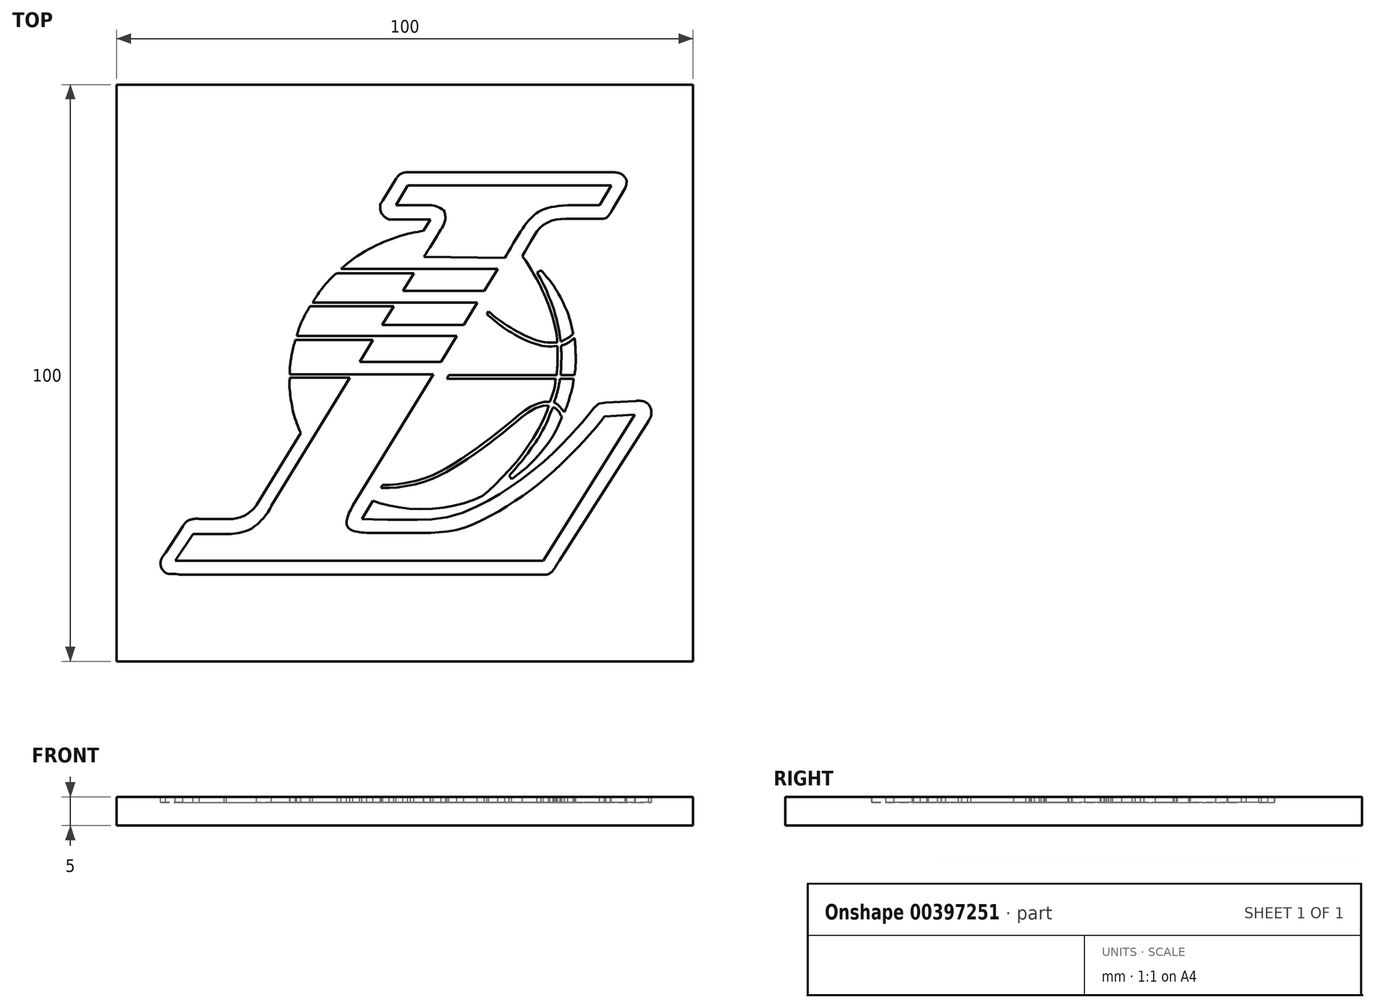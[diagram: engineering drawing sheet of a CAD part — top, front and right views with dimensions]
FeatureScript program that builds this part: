
annotation { "Feature Type Name" : "Feature", "Feature Type Description" : "" }
export const myFeature = defineFeature(function(context is Context, id is Id, definition is map)
    precondition{}
    {
        {
            var Q0;
            Q0=qCreatedBy(makeId("Top.planeOp"),FACE);
            var sketch = newSketch(context, id + "F0", { "sketchPlane" : qUnion([Q0])});
            skLineSegment(sketch, "E0.bottom", {"start": v(-100, 100) * mm, "end": v(0, 100) * mm});
            skLineSegment(sketch, "E0.top", {"start": v(-100, 0) * mm, "end": v(0, 0) * mm});
            skLineSegment(sketch, "E0.left", {"start": v(-100, 100) * mm, "end": v(-100, 0) * mm});
            skLineSegment(sketch, "E0.right", {"start": v(0, 100) * mm, "end": v(0, 0) * mm});
            skSolve(sketch);
        }
        {
            var Q0;
            Q0=makeQuery(id+"F0.imprint","IMPRINT",FACE,{"disambiguationData":[TD([[makeQuery(id+"F0.imprint","IMPRINT",EDGE,{"derivedFrom":sQuery(id+"F0.wireOp",EDGE,"E0.bottom")}),-1.0]])]});
            extrude(context, id + "F1", {"entities" : qUnion([Q0]), "depth" : 5 * mm});
        }
        {
            var Q0;
            Q0=makeQuery(id+"F1.opExtrude","CAP_FACE",FACE,{"disambiguationData":[OSD([sQuery(id+"F0.wireOp",EDGE,"E0.bottom"),sQuery(id+"F0.wireOp",EDGE,"E0.top"),sQuery(id+"F0.wireOp",EDGE,"E0.left"),sQuery(id+"F0.wireOp",EDGE,"E0.right")])],"isStart":false});
            var sketch = newSketch(context, id + "F2", { "sketchPlane" : qUnion([Q0])});
            skLineSegment(sketch, "E1", {"start": v(-49.48, 82.53) * mm, "end": v(-14.17, 82.53) * mm});
            skLineSegment(sketch, "E2", {"start": v(-14.17, 82.53) * mm, "end": v(-16.2, 79.12) * mm});
            skLineSegment(sketch, "E3", {"start": v(-49.48, 82.53) * mm, "end": v(-51.53, 79.12) * mm});
            skLineSegment(sketch, "E4", {"start": v(-51.53, 79.12) * mm, "end": v(-16.2, 79.12) * mm});
            skFitSpline(sketch, "E5", {"points": [v(-46.17, 79.12) * mm, v(-43.82, 78.6) * mm, v(-43.2, 78.1) * mm, v(-42.95, 77) * mm, v(-43.14, 75.96) * mm, v(-43.56, 75.18) * mm, v(-44.92, 72.94) * mm, v(-46.68, 70.13) * mm], "startDerivative": vector(19.55, 0) * mm, "endDerivative": vector(-5.5, -9.14) * mm});
            skLineSegment(sketch, "E6", {"start": v(-46.68, 70.13) * mm, "end": v(-32.67, 69.96) * mm});
            skFitSpline(sketch, "E7", {"points": [v(-32.67, 69.96) * mm, v(-31.75, 71.5) * mm, v(-30.34, 73.85) * mm, v(-29.38, 75.31) * mm, v(-28.57, 76.38) * mm, v(-27.56, 77.39) * mm, v(-26.45, 78.15) * mm, v(-25.23, 78.6) * mm, v(-24.02, 78.85) * mm, v(-21.74, 79.12) * mm], "startDerivative": vector(6.47, 8.78) * mm, "endDerivative": vector(18.83, 1.98) * mm});
            skLineSegment(sketch, "E8", {"start": v(-32.67, 69.96) * mm, "end": v(-59, 27) * mm});
            skLineSegment(sketch, "E9", {"start": v(-46.68, 70.13) * mm, "end": v(-73.1, 27) * mm});
            skLineSegment(sketch, "E10", {"start": v(-57.84, 51.91) * mm, "end": v(-43.73, 51.91) * mm});
            skLineSegment(sketch, "E11", {"start": v(-40.98, 56.4) * mm, "end": v(-55.1, 56.4) * mm});
            skLineSegment(sketch, "E12", {"start": v(-53.92, 58.3) * mm, "end": v(-39.8, 58.3) * mm});
            skLineSegment(sketch, "E13", {"start": v(-51.53, 62.22) * mm, "end": v(-37.42, 62.22) * mm});
            skLineSegment(sketch, "E14", {"start": v(-50.31, 64.2) * mm, "end": v(-36.2, 64.2) * mm});
            skLineSegment(sketch, "E15", {"start": v(-47.98, 68.01) * mm, "end": v(-33.86, 68.01) * mm});
            skLineSegment(sketch, "E16", {"start": v(-47.98, 68.01) * mm, "end": v(-61.05, 68.01) * mm});
            skLineSegment(sketch, "E17", {"start": v(-48.42, 67.3) * mm, "end": v(-61.7, 67.3) * mm});
            skLineSegment(sketch, "E18", {"start": v(-51.53, 62.22) * mm, "end": v(-65.98, 62.22) * mm});
            skLineSegment(sketch, "E19", {"start": v(-51.91, 61.59) * mm, "end": v(-66.43, 61.59) * mm});
            skLineSegment(sketch, "E20", {"start": v(-55.1, 56.4) * mm, "end": v(-68.73, 56.4) * mm});
            skLineSegment(sketch, "E21", {"start": v(-55.51, 55.72) * mm, "end": v(-69, 55.72) * mm});
            skLineSegment(sketch, "E22", {"start": v(-45.03, 49.78) * mm, "end": v(-59.15, 49.78) * mm});
            skLineSegment(sketch, "E23", {"start": v(-59.15, 49.78) * mm, "end": v(-69.91, 49.78) * mm});
            skLineSegment(sketch, "E24", {"start": v(-59.52, 49.18) * mm, "end": v(-69.91, 49.18) * mm});
            skLineSegment(sketch, "E25", {"start": v(-68.06, 39.57) * mm, "end": v(-75.7, 27.09) * mm});
            skFitSpline(sketch, "E26", {"points": [v(-68.06, 39.57) * mm, v(-68.74, 41.27) * mm, v(-69.33, 43.15) * mm, v(-69.67, 44.93) * mm, v(-69.93, 46.8) * mm, v(-70.01, 48.25) * mm, v(-69.91, 49.18) * mm], "startDerivative": vector(-3.92, 9.44) * mm, "endDerivative": vector(1.08, 6.98) * mm});
            skFitSpline(sketch, "E27", {"points": [v(-69.91, 49.78) * mm, v(-69.91, 51.06) * mm, v(-69.59, 53.27) * mm, v(-69, 55.72) * mm], "startDerivative": vector(-0.17, 4.43) * mm, "endDerivative": vector(1.7, 6.44) * mm});
            skFitSpline(sketch, "E28", {"points": [v(-68.73, 56.4) * mm, v(-68.39, 57.62) * mm, v(-67.76, 59.14) * mm, v(-67.06, 60.5) * mm, v(-66.43, 61.59) * mm], "startDerivative": vector(1.27, 5.03) * mm, "endDerivative": vector(2.65, 4.48) * mm});
            skFitSpline(sketch, "E29", {"points": [v(-65.98, 62.22) * mm, v(-65.3, 63.32) * mm, v(-64.37, 64.65) * mm, v(-63.47, 65.7) * mm, v(-62.22, 66.99) * mm, v(-61.7, 67.3) * mm], "startDerivative": vector(3.14, 5.34) * mm, "endDerivative": vector(3.42, 1.55) * mm});
            skFitSpline(sketch, "E30", {"points": [v(-61.05, 68.01) * mm, v(-58.93, 69.78) * mm, v(-56.04, 71.57) * mm, v(-53.31, 72.85) * mm, v(-50.42, 73.87) * mm, v(-48.2, 74.38) * mm, v(-46.76, 74.64) * mm], "startDerivative": vector(11.67, 10.43) * mm, "endDerivative": vector(11.08, 1.87) * mm});
            skLineSegment(sketch, "E31", {"start": v(-52.76, 76.64) * mm, "end": v(-45.58, 76.64) * mm});
            skLineSegment(sketch, "E32", {"start": v(-46.76, 74.64) * mm, "end": v(-45.58, 76.64) * mm});
            skLineSegment(sketch, "E33", {"start": v(-51.54, 83.66) * mm, "end": v(-53.82, 79.91) * mm});
            skFitSpline(sketch, "E34", {"points": [v(-53.82, 79.91) * mm, v(-54.18, 79.35) * mm, v(-54.28, 78.75) * mm, v(-54.18, 78.09) * mm, v(-54.05, 77.68) * mm, v(-53.82, 77.42) * mm, v(-53.56, 77.15) * mm, v(-53.2, 76.87) * mm, v(-53, 76.75) * mm, v(-52.76, 76.64) * mm], "startDerivative": vector(-2.98, -3.96) * mm, "endDerivative": vector(2.95, -1.16) * mm});
            skLineSegment(sketch, "E35", {"start": v(-49, 84.82) * mm, "end": v(-14.34, 84.82) * mm});
            skLineSegment(sketch, "E36", {"start": v(-11.8, 82.06) * mm, "end": v(-14, 78.3) * mm});
            skLineSegment(sketch, "E37", {"start": v(-56.6, 22.28) * mm, "end": v(-45.52, 22.28) * mm});
            skLineSegment(sketch, "E38", {"start": v(-10.13, 42.74) * mm, "end": v(-26.02, 17.47) * mm});
            skLineSegment(sketch, "E39", {"start": v(-89.8, 17.47) * mm, "end": v(-26.02, 17.47) * mm});
            skLineSegment(sketch, "E40", {"start": v(-89.8, 17.47) * mm, "end": v(-86.68, 22.04) * mm});
            skLineSegment(sketch, "E41", {"start": v(-86.68, 22.04) * mm, "end": v(-80.9, 22.04) * mm});
            skFitSpline(sketch, "E42", {"points": [v(-59, 27) * mm, v(-59.35, 26.34) * mm, v(-59.7, 25.7) * mm, v(-59.88, 25.14) * mm, v(-60.02, 24.65) * mm, v(-60.1, 24.28) * mm, v(-60.11, 23.84) * mm, v(-60, 23.49) * mm, v(-59.79, 23.12) * mm, v(-59.37, 22.81) * mm, v(-58.9, 22.63) * mm, v(-58.23, 22.44) * mm, v(-57.56, 22.33) * mm, v(-56.6, 22.28) * mm], "startDerivative": vector(-3.93, -7.43) * mm, "endDerivative": vector(10.18, -0.27) * mm});
            skFitSpline(sketch, "E43", {"points": [v(-45.52, 22.28) * mm, v(-43.09, 22.47) * mm, v(-40.43, 22.94) * mm, v(-37.82, 23.87) * mm, v(-35.16, 25.2) * mm, v(-32.51, 26.72) * mm, v(-30.1, 28.32) * mm, v(-27.4, 30.23) * mm, v(-24.75, 32.5) * mm, v(-22.17, 34.91) * mm, v(-19.36, 37.76) * mm, v(-17.68, 39.6) * mm, v(-15.77, 41.9) * mm, v(-15.38, 42.48) * mm], "startDerivative": vector(33.48, 2) * mm, "endDerivative": vector(7.48, 12.44) * mm});
            skLineSegment(sketch, "E44", {"start": v(-15.38, 42.48) * mm, "end": v(-10.13, 42.74) * mm});
            skFitSpline(sketch, "E45", {"points": [v(-80.9, 22.04) * mm, v(-79.3, 22.19) * mm, v(-77.26, 22.67) * mm, v(-75.85, 23.54) * mm, v(-74.43, 24.92) * mm, v(-73.5, 26.22) * mm, v(-73.1, 27) * mm], "startDerivative": vector(9.14, 0.62) * mm, "endDerivative": vector(2.76, 6.02) * mm});
            skLineSegment(sketch, "E46", {"start": v(-88.77, 15.03) * mm, "end": v(-27.84, 15.03) * mm});
            skLineSegment(sketch, "E47", {"start": v(-85.62, 24.7) * mm, "end": v(-81.32, 24.7) * mm});
            skLineSegment(sketch, "E48", {"start": v(-88.48, 23.4) * mm, "end": v(-91.49, 18.83) * mm});
            skFitSpline(sketch, "E49", {"points": [v(-81.32, 24.7) * mm, v(-79.75, 24.7) * mm, v(-78.49, 24.98) * mm, v(-77.37, 25.52) * mm, v(-76.23, 26.45) * mm, v(-75.7, 27.09) * mm], "startDerivative": vector(7.25, -0.32) * mm, "endDerivative": vector(2.8, 3.76) * mm});
            skFitSpline(sketch, "E50", {"points": [v(-88.48, 23.4) * mm, v(-88.09, 24) * mm, v(-87.62, 24.39) * mm, v(-87.13, 24.57) * mm, v(-86.55, 24.7) * mm, v(-85.62, 24.7) * mm], "startDerivative": vector(1.8, 2.98) * mm, "endDerivative": vector(4.19, -0.18) * mm});
            skFitSpline(sketch, "E51", {"points": [v(-91.49, 18.83) * mm, v(-91.8, 18.38) * mm, v(-92.15, 17.87) * mm, v(-92.33, 17.38) * mm, v(-92.38, 16.9) * mm, v(-92.29, 16.34) * mm, v(-91.98, 15.85) * mm, v(-91.49, 15.36) * mm, v(-90.7, 15.15) * mm, v(-89.4, 15.1) * mm, v(-88.77, 15.03) * mm], "startDerivative": vector(-3.3, -4.87) * mm, "endDerivative": vector(5.77, 0.02) * mm});
            skLineSegment(sketch, "E52", {"start": v(-7.72, 41.71) * mm, "end": v(-23.21, 17.44) * mm});
            skFitSpline(sketch, "E53", {"points": [v(-27.84, 15.03) * mm, v(-26.1, 15.03) * mm, v(-25.32, 15.03) * mm, v(-24.3, 15.75) * mm, v(-23.77, 16.55) * mm, v(-23.21, 17.44) * mm], "startDerivative": vector(12.74, 0) * mm, "endDerivative": vector(4.78, 7.53) * mm});
            skLineSegment(sketch, "E54", {"start": v(-15.16, 44.88) * mm, "end": v(-10, 45.13) * mm});
            skFitSpline(sketch, "E55", {"points": [v(-10, 45.13) * mm, v(-8.88, 45.13) * mm, v(-8.02, 44.78) * mm, v(-7.41, 44.02) * mm, v(-7.26, 43) * mm, v(-7.35, 42.38) * mm, v(-7.72, 41.71) * mm], "startDerivative": vector(6.23, 0.44) * mm, "endDerivative": vector(-4.55, -7.7) * mm});
            skFitSpline(sketch, "E56", {"points": [v(-15.16, 44.88) * mm, v(-16.12, 44.77) * mm, v(-16.67, 44.44) * mm, v(-17.45, 43.69) * mm, v(-18.53, 42.27) * mm, v(-19.68, 40.92) * mm, v(-20.54, 40) * mm, v(-22.03, 38.4) * mm, v(-23.93, 36.47) * mm, v(-26.25, 34.36) * mm, v(-29.29, 31.92) * mm, v(-31.94, 30.02) * mm, v(-34.8, 28.22) * mm, v(-37.77, 26.71) * mm, v(-42.05, 25.12) * mm, v(-46.65, 24.57) * mm, v(-50.2, 24.54) * mm, v(-54.86, 24.6) * mm, v(-57.45, 24.66) * mm], "startDerivative": vector(-30.95, -1.07) * mm, "endDerivative": vector(-40.45, -0.22) * mm});
            skLineSegment(sketch, "E57", {"start": v(-57.45, 24.66) * mm, "end": v(-55.54, 27.82) * mm});
            skFitSpline(sketch, "E58", {"points": [v(-55.54, 27.82) * mm, v(-54.21, 27.4) * mm, v(-51.95, 26.84) * mm, v(-49.5, 26.5) * mm, v(-46.17, 26.38) * mm, v(-43.2, 26.69) * mm, v(-40.63, 27.16) * mm, v(-37.7, 28.1) * mm, v(-36.15, 28.95) * mm, v(-34.86, 30.12) * mm, v(-33.22, 31.76) * mm, v(-31.3, 33.79) * mm, v(-29.8, 35.69) * mm, v(-28.42, 37.64) * mm, v(-27.18, 39.6) * mm, v(-25.95, 41.97) * mm, v(-25.14, 43.9) * mm, v(-25.05, 44.35) * mm], "startDerivative": vector(26.43, -9.1) * mm, "endDerivative": vector(1.68, 14.14) * mm});
            skFitSpline(sketch, "E59", {"points": [v(-25.05, 44.35) * mm, v(-25.56, 44.35) * mm, v(-26.25, 44.27) * mm, v(-27.34, 43.92) * mm, v(-28.33, 43.33) * mm, v(-29.47, 42.53) * mm, v(-30.31, 41.84) * mm, v(-31.17, 41.1) * mm, v(-32.12, 40.34) * mm, v(-32.89, 39.67) * mm, v(-34.1, 38.76) * mm, v(-35.01, 38.05) * mm, v(-36.3, 37.08) * mm, v(-37, 36.58) * mm, v(-37.95, 35.9) * mm, v(-39.34, 34.98) * mm, v(-40.4, 34.26) * mm, v(-41.25, 33.73) * mm, v(-42.4, 33.06) * mm, v(-43.26, 32.56) * mm, v(-44.15, 32.13) * mm, v(-44.94, 31.76) * mm, v(-46.52, 31.2) * mm, v(-48, 30.74) * mm, v(-49.42, 30.46) * mm, v(-50.74, 30.24) * mm, v(-51.86, 30.1) * mm, v(-52.84, 30.06) * mm, v(-54.16, 30.04) * mm], "startDerivative": vector(-21.15, 0.4) * mm, "endDerivative": vector(-36.26, -0.52) * mm});
            skLineSegment(sketch, "E60", {"start": v(-54.16, 30.04) * mm, "end": v(-53.86, 30.56) * mm});
            skFitSpline(sketch, "E61", {"points": [v(-53.86, 30.56) * mm, v(-53.11, 30.56) * mm, v(-52.06, 30.62) * mm, v(-50.65, 30.79) * mm, v(-49.07, 31.06) * mm, v(-47.57, 31.41) * mm, v(-46.33, 31.85) * mm, v(-45.1, 32.29) * mm, v(-44.2, 32.72) * mm, v(-43.03, 33.35) * mm, v(-41.92, 34) * mm, v(-40.7, 34.8) * mm, v(-39.63, 35.48) * mm, v(-38.38, 36.37) * mm, v(-36.94, 37.37) * mm, v(-35.85, 38.18) * mm, v(-34.72, 39.04) * mm, v(-33.54, 39.94) * mm, v(-32.1, 41.17) * mm, v(-31.07, 42) * mm, v(-30.24, 42.68) * mm, v(-29.43, 43.34) * mm, v(-28.64, 43.88) * mm, v(-27.85, 44.31) * mm, v(-26.86, 44.7) * mm, v(-26.12, 44.93) * mm, v(-25.36, 45) * mm, v(-24.87, 45) * mm], "startDerivative": vector(24.65, -0.24) * mm, "endDerivative": vector(19.44, -0.15) * mm});
            skFitSpline(sketch, "E62", {"points": [v(-24.87, 45) * mm, v(-24.5, 46) * mm, v(-24.11, 47.14) * mm, v(-23.93, 48.07) * mm, v(-23.84, 49) * mm], "startDerivative": vector(1.4, 3.85) * mm, "endDerivative": vector(0.33, 3.96) * mm});
            skLineSegment(sketch, "E63", {"start": v(-23.84, 49) * mm, "end": v(-42.68, 49) * mm});
            skLineSegment(sketch, "E64", {"start": v(-42.68, 49) * mm, "end": v(-42.35, 49.61) * mm});
            skLineSegment(sketch, "E65", {"start": v(-42.35, 49.61) * mm, "end": v(-23.67, 49.61) * mm});
            skLineSegment(sketch, "E66", {"start": v(-23.08, 49) * mm, "end": v(-20.7, 49) * mm});
            skLineSegment(sketch, "E67", {"start": v(-22.96, 49.61) * mm, "end": v(-20.59, 49.61) * mm});
            skFitSpline(sketch, "E68", {"points": [v(-23.08, 49) * mm, v(-23.26, 47.95) * mm, v(-23.54, 46.78) * mm, v(-23.8, 45.8) * mm, v(-24.12, 44.83) * mm], "startDerivative": vector(-0.63, -4.14) * mm, "endDerivative": vector(-1.32, -4.02) * mm});
            skFitSpline(sketch, "E69", {"points": [v(-24.12, 44.83) * mm, v(-23.65, 44.63) * mm, v(-23.08, 44.09) * mm, v(-22.6, 43.54) * mm, v(-22.33, 43.23) * mm], "startDerivative": vector(2.04, -0.6) * mm, "endDerivative": vector(1.22, -1.4) * mm});
            skFitSpline(sketch, "E70", {"points": [v(-22.33, 43.23) * mm, v(-21.82, 44.44) * mm, v(-21.47, 45.6) * mm, v(-21.12, 46.78) * mm, v(-20.84, 47.99) * mm, v(-20.7, 49) * mm], "startDerivative": vector(2.62, 5.78) * mm, "endDerivative": vector(0.63, 5.36) * mm});
            skFitSpline(sketch, "E71", {"points": [v(-20.59, 49.61) * mm, v(-20.41, 50.88) * mm, v(-20.37, 52.63) * mm, v(-20.41, 54.33) * mm, v(-20.56, 56.05) * mm], "startDerivative": vector(0.93, 5.44) * mm, "endDerivative": vector(-0.57, 6.09) * mm});
            skFitSpline(sketch, "E72", {"points": [v(-20.56, 56.05) * mm, v(-21.05, 55.67) * mm, v(-21.46, 55.36) * mm, v(-22.2, 54.97) * mm, v(-22.9, 54.77) * mm], "startDerivative": vector(-2.11, -1.65) * mm, "endDerivative": vector(-2.55, -0.65) * mm});
            skFitSpline(sketch, "E73", {"points": [v(-22.9, 54.77) * mm, v(-22.87, 54.21) * mm, v(-22.84, 53.03) * mm, v(-22.9, 51.28) * mm, v(-22.96, 49.61) * mm], "startDerivative": vector(0.52, -4) * mm, "endDerivative": vector(-0.57, -10.64) * mm});
            skFitSpline(sketch, "E74", {"points": [v(-23.67, 49.61) * mm, v(-23.55, 51.1) * mm, v(-23.53, 52.4) * mm, v(-23.51, 53.43) * mm, v(-23.54, 54.28) * mm, v(-23.58, 54.7) * mm], "startDerivative": vector(0.57, 6.1) * mm, "endDerivative": vector(-0.34, 2.88) * mm});
            skFitSpline(sketch, "E75", {"points": [v(-23.58, 54.7) * mm, v(-24.54, 54.6) * mm, v(-26.03, 54.7) * mm, v(-27.58, 55.11) * mm, v(-29.37, 55.83) * mm, v(-30.67, 56.5) * mm, v(-32.43, 57.57) * mm, v(-33.78, 58.53) * mm, v(-34.57, 59.2) * mm, v(-35.75, 60.2) * mm], "startDerivative": vector(-10.17, -1.32) * mm, "endDerivative": vector(-11.24, 9.37) * mm});
            skFitSpline(sketch, "E76", {"points": [v(-35.75, 60.2) * mm, v(-35.47, 60.66) * mm], "startDerivative": vector(0.28, 0.46) * mm, "endDerivative": vector(0.28, 0.46) * mm});
            skFitSpline(sketch, "E77", {"points": [v(-35.47, 60.66) * mm, v(-35.1, 60.38) * mm, v(-34.4, 59.78) * mm, v(-32.8, 58.6) * mm, v(-30.8, 57.39) * mm, v(-28.77, 56.32) * mm, v(-26.84, 55.6) * mm, v(-25.22, 55.3) * mm, v(-23.58, 55.25) * mm], "startDerivative": vector(5.28, -3.74) * mm, "endDerivative": vector(13, 0.02) * mm});
            skFitSpline(sketch, "E78", {"points": [v(-23.58, 55.25) * mm, v(-23.67, 56.65) * mm, v(-24.1, 58.66) * mm, v(-24.7, 60.75) * mm, v(-25.3, 62.42) * mm, v(-25.91, 63.8) * mm, v(-26.56, 65.23) * mm, v(-27.56, 67.04) * mm, v(-28.53, 68.69) * mm, v(-29.2, 69.7) * mm, v(-29.6, 70.27) * mm], "startDerivative": vector(-0.33, 14.26) * mm, "endDerivative": vector(-5.72, 7.98) * mm});
            skFitSpline(sketch, "E79", {"points": [v(-29.6, 70.27) * mm, v(-28.55, 72.13) * mm, v(-27.17, 74.43) * mm, v(-26.18, 75.48) * mm, v(-24.94, 76.26) * mm, v(-23.3, 76.66) * mm, v(-21.53, 76.72) * mm, v(-18.44, 76.72) * mm, v(-16.47, 76.72) * mm, v(-15.68, 76.72) * mm, v(-15.03, 76.92) * mm, v(-14.5, 77.5) * mm, v(-14, 78.3) * mm], "startDerivative": vector(10.19, 17.87) * mm, "endDerivative": vector(7.5, 12.46) * mm});
            skFitSpline(sketch, "E80", {"points": [v(-11.8, 82.06) * mm, v(-11.55, 83.28) * mm, v(-12.08, 84.2) * mm, v(-12.8, 84.66) * mm, v(-14.34, 84.82) * mm], "startDerivative": vector(1.8, 4.87) * mm, "endDerivative": vector(-5.92, 0.16) * mm});
            skFitSpline(sketch, "E81", {"points": [v(-51.54, 83.66) * mm, v(-51.24, 84.07) * mm, v(-50.73, 84.5) * mm, v(-50, 84.78) * mm, v(-49, 84.82) * mm], "startDerivative": vector(1.32, 2) * mm, "endDerivative": vector(3.52, -0.06) * mm});
            skFitSpline(sketch, "E82", {"points": [v(-31.43, 31.58) * mm, v(-29.5, 33.1) * mm, v(-27.43, 35.07) * mm, v(-24.7, 38.46) * mm, v(-23.49, 40.63) * mm, v(-22.73, 42.3) * mm], "startDerivative": vector(10.3, 7.88) * mm, "endDerivative": vector(4.47, 10.09) * mm});
            skFitSpline(sketch, "E83", {"points": [v(-22.73, 42.3) * mm, v(-23.23, 43.22) * mm, v(-23.59, 43.62) * mm, v(-24.2, 44.03) * mm, v(-24.35, 44.08) * mm], "startDerivative": vector(-1.58, 3) * mm, "endDerivative": vector(-0.93, 0.2) * mm});
            skFitSpline(sketch, "E84", {"points": [v(-24.3, 44.07) * mm, v(-24.89, 42.7) * mm, v(-25.45, 41.33) * mm, v(-26.42, 39.47) * mm, v(-27.07, 38.31) * mm, v(-27.94, 37.15) * mm, v(-28.75, 35.97) * mm, v(-29.93, 34.49) * mm, v(-30.73, 33.52) * mm, v(-31.91, 32.18) * mm], "startDerivative": vector(-5.64, -12.83) * mm, "endDerivative": vector(-10.65, -11.97) * mm});
            skLineSegment(sketch, "E85", {"start": v(-31.91, 32.18) * mm, "end": v(-31.43, 31.58) * mm});
            skFitSpline(sketch, "E86", {"points": [v(-22.95, 55.44) * mm, v(-22.34, 55.74) * mm, v(-21.58, 56.15) * mm, v(-20.82, 56.76) * mm], "startDerivative": vector(1.95, 1) * mm, "endDerivative": vector(2.05, 1.8) * mm});
            skFitSpline(sketch, "E87", {"points": [v(-20.82, 56.76) * mm, v(-21.1, 58.12) * mm, v(-21.46, 59.48) * mm, v(-21.86, 60.68) * mm, v(-22.43, 61.95) * mm, v(-23.02, 63.16) * mm, v(-23.7, 64.33) * mm, v(-24.38, 65.4) * mm, v(-24.95, 66.13) * mm, v(-25.7, 67.03) * mm, v(-26.4, 67.82) * mm], "startDerivative": vector(-2.5, 12.88) * mm, "endDerivative": vector(-7.48, 8.32) * mm});
            skFitSpline(sketch, "E88", {"points": [v(-27.08, 67.44) * mm, v(-26.31, 66.1) * mm, v(-25.42, 64.24) * mm, v(-24.85, 62.85) * mm, v(-24.33, 61.54) * mm, v(-23.93, 60.25) * mm, v(-23.51, 58.6) * mm, v(-23.18, 56.98) * mm, v(-23.03, 55.9) * mm, v(-22.95, 55.44) * mm], "startDerivative": vector(6.4, -10.71) * mm, "endDerivative": vector(1.27, -6.42) * mm});
            skLineSegment(sketch, "E89", {"start": v(-27.08, 67.44) * mm, "end": v(-26.4, 67.82) * mm});
            skSolve(sketch);
        }
        {
            var Q0;
            Q0=makeQuery(id+"F2.imprint","IMPRINT",FACE,{"disambiguationData":[TD([[makeQuery(id+"F2.imprint","IMPRINT",EDGE,{"derivedFrom":sQuery(id+"F2.wireOp",EDGE,"E1")}),1.0]])]});
            var Q1;
            Q1=makeQuery(id+"F2.imprint","IMPRINT",FACE,{"disambiguationData":[TD([[makeQuery(id+"F2.imprint","IMPRINT",EDGE,{"derivedFrom":sQuery(id+"F2.wireOp",EDGE,"E67")}),1.0]])]});
            var Q2;
            Q2=makeQuery(id+"F2.imprint","IMPRINT",FACE,{"disambiguationData":[TD([[makeQuery(id+"F2.imprint","IMPRINT",EDGE,{"derivedFrom":sQuery(id+"F2.wireOp",EDGE,"E86")}),1.0]])]});
            var Q3;
            {var subQ0=sQuery(id+"F2.wireOp",EDGE,"E82");Q3=makeQuery(id+"F2.imprint","IMPRINT",FACE,{"disambiguationData":[TD([[makeQuery(id+"F2.imprint","IMPRINT",EDGE,{"derivedFrom":subQ0}),1.0]])]});}
            var Q4;
            Q4=makeQuery(id+"F2.imprint","IMPRINT",FACE,{"disambiguationData":[TD([[makeQuery(id+"F2.imprint","IMPRINT",EDGE,{"derivedFrom":sQuery(id+"F2.wireOp",EDGE,"E66")}),-1.0]])]});
            var Q5;
            {var subQ0=sQuery(id+"F2.wireOp",EDGE,"E10");Q5=makeQuery(id+"F2.imprint","IMPRINT",FACE,{"disambiguationData":[TD([[makeQuery(id+"F2.imprint","IMPRINT",EDGE,{"derivedFrom":subQ0}),-1.0]])]});}
            var Q6;
            {var subQ0=sQuery(id+"F2.wireOp",EDGE,"E11");Q6=makeQuery(id+"F2.imprint","IMPRINT",FACE,{"disambiguationData":[TD([[makeQuery(id+"F2.imprint","IMPRINT",EDGE,{"derivedFrom":subQ0}),-1.0]])]});}
            var Q7;
            {var subQ1=sQuery(id+"F2.wireOp",EDGE,"E19");Q7=makeQuery(id+"F2.imprint","IMPRINT",FACE,{"disambiguationData":[TD([[makeQuery(id+"F2.imprint","IMPRINT",EDGE,{"derivedFrom":subQ1}),1.0]])]});}
            var Q8;
            {var subQ3=sQuery(id+"F2.wireOp",EDGE,"E21");Q8=makeQuery(id+"F2.imprint","IMPRINT",FACE,{"disambiguationData":[TD([[makeQuery(id+"F2.imprint","IMPRINT",EDGE,{"derivedFrom":subQ3}),1.0]])]});}
            var Q9;
            {var subQ1=sQuery(id+"F2.wireOp",EDGE,"E17");Q9=makeQuery(id+"F2.imprint","IMPRINT",FACE,{"disambiguationData":[TD([[makeQuery(id+"F2.imprint","IMPRINT",EDGE,{"derivedFrom":subQ1}),1.0]])]});}
            var Q10;
            {var subQ0=sQuery(id+"F2.wireOp",EDGE,"E13");Q10=makeQuery(id+"F2.imprint","IMPRINT",FACE,{"disambiguationData":[TD([[makeQuery(id+"F2.imprint","IMPRINT",EDGE,{"derivedFrom":subQ0}),1.0]])]});}
            var Q11;
            {var subQ0=sQuery(id+"F2.wireOp",EDGE,"E6");Q11=makeQuery(id+"F2.imprint","IMPRINT",FACE,{"disambiguationData":[TD([[makeQuery(id+"F2.imprint","IMPRINT",EDGE,{"derivedFrom":subQ0}),-1.0]])]});}
            extrude(context, id + "F3", {"entities" : qUnion([Q0, Q1, Q2, Q3, Q4, Q5, Q6, Q7, Q8, Q9, Q10, Q11]), "operationType" : NewBodyOperationType.REMOVE, "oppositeDirection" : true, "depth" : 1 * mm});
        }
    });
